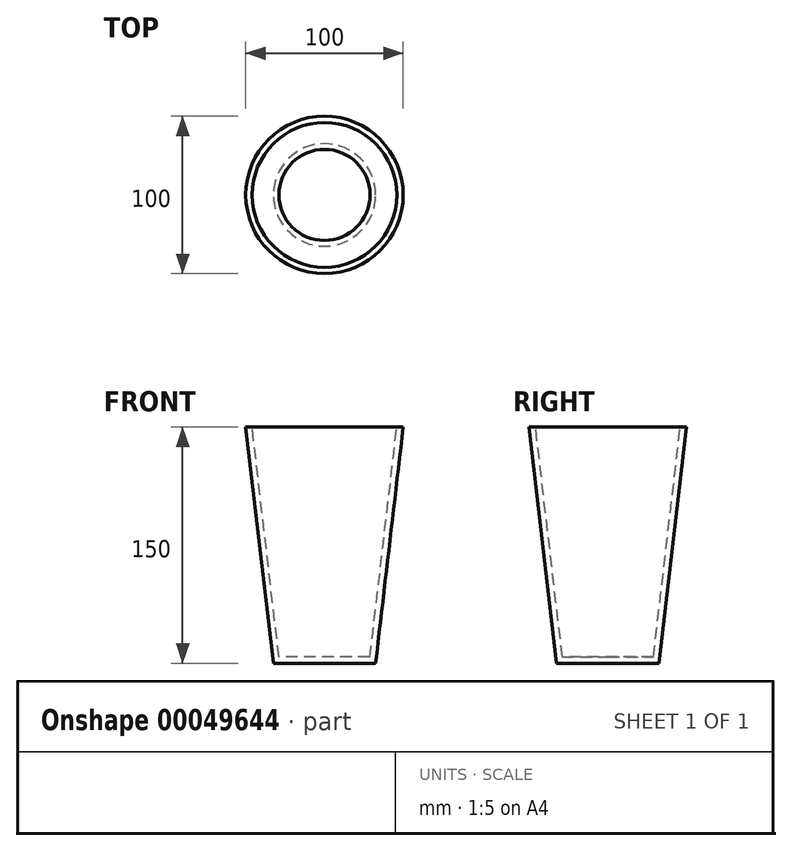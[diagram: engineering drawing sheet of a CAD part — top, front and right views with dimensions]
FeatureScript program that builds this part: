
annotation { "Feature Type Name" : "Feature", "Feature Type Description" : "" }
export const myFeature = defineFeature(function(context is Context, id is Id, definition is map)
    precondition{}
    {
        {
            var Q0;
            Q0=qCreatedBy(makeId("Right.planeOp"),FACE);
            var sketch = newSketch(context, id + "F0", { "sketchPlane" : qUnion([Q0])});
            skLineSegment(sketch, "E0", {"start": v(0, 0) * mm, "end": v(32.5, 0) * mm});
            skLineSegment(sketch, "E1", {"start": v(32.5, 0) * mm, "end": v(50, 150) * mm});
            skLineSegment(sketch, "E2", {"start": v(50, 150) * mm, "end": v(45.97, 150) * mm});
            skLineSegment(sketch, "E3", {"start": v(45.97, 150) * mm, "end": v(28.94, 4) * mm});
            skLineSegment(sketch, "E4", {"start": v(28.94, 4) * mm, "end": v(0, 4) * mm});
            skLineSegment(sketch, "E5", {"start": v(0, 4) * mm, "end": v(0, 0) * mm});
            skSolve(sketch);
        }
        {
            var Q0;
            Q0 = qSketchRegion(id + "F0", true);
            var Q1;
            Q1=sQuery(id+"F0.wireOp",EDGE,"E5");
            revolve(context, id + "F1", {"entities" : qUnion([Q0]), "axis" : qUnion([Q1]), "revolveType" : RevolveType.FULL});
        }
    });
